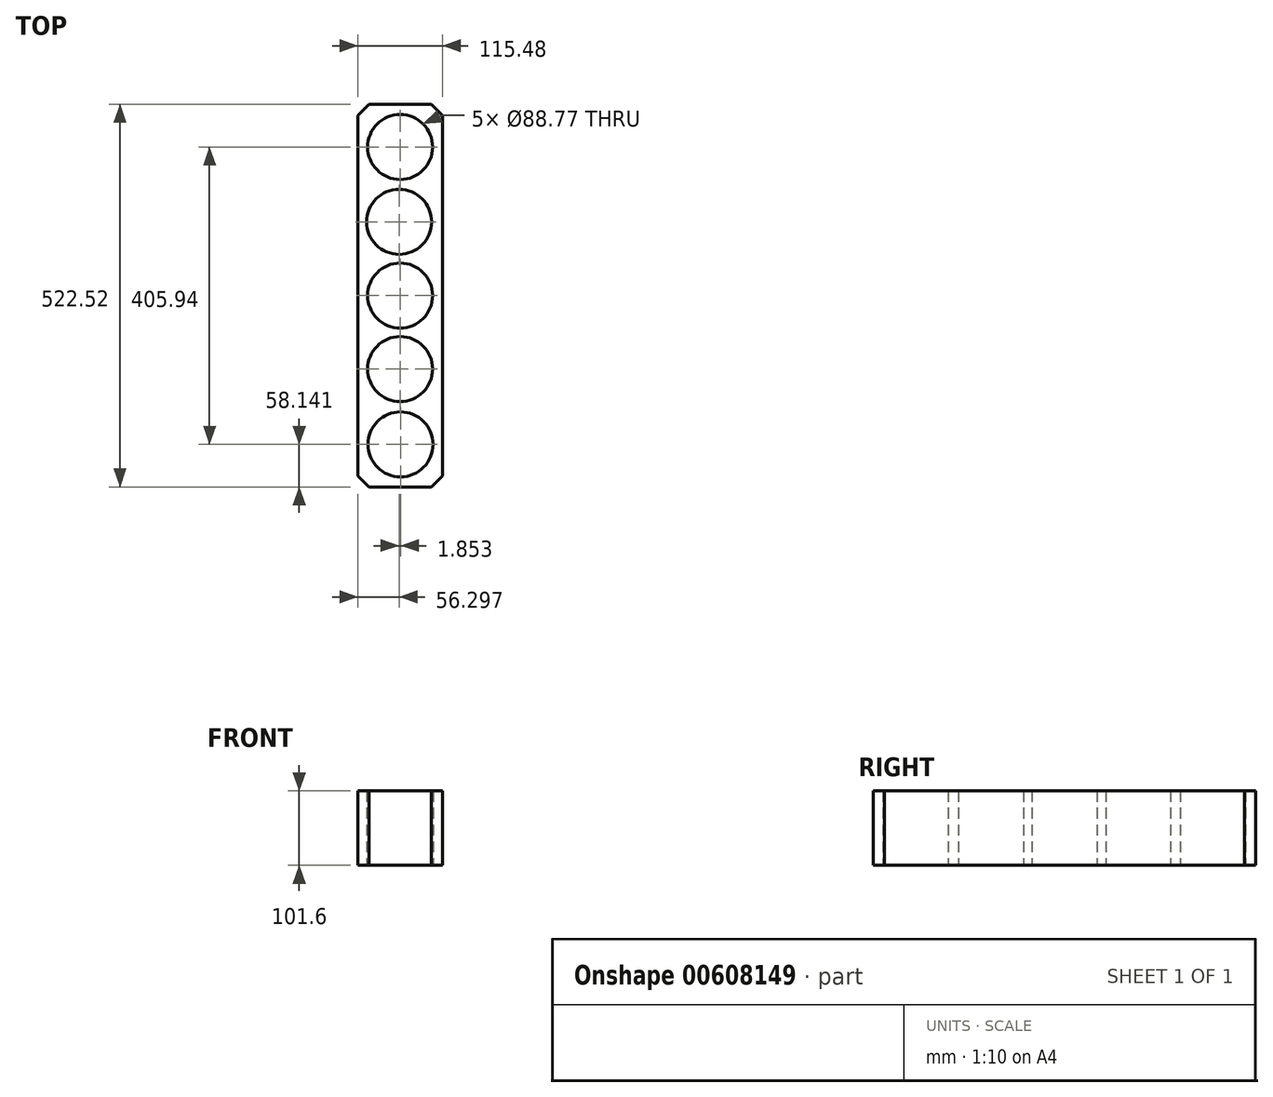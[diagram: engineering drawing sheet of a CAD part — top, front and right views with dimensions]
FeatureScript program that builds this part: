
annotation { "Feature Type Name" : "Feature", "Feature Type Description" : "" }
export const myFeature = defineFeature(function(context is Context, id is Id, definition is map)
    precondition{}
    {
        {
            var Q0;
            Q0=qCreatedBy(makeId("Top.planeOp"),FACE);
            var sketch = newSketch(context, id + "F0", { "sketchPlane" : qUnion([Q0])});
            skLineSegment(sketch, "E0.bottom", {"start": v(-57.74, 261.26) * mm, "end": v(57.74, 261.26) * mm});
            skLineSegment(sketch, "E0.top", {"start": v(-57.74, -261.26) * mm, "end": v(57.74, -261.26) * mm});
            skLineSegment(sketch, "E0.left", {"start": v(-57.74, 261.26) * mm, "end": v(-57.74, -261.26) * mm});
            skLineSegment(sketch, "E0.right", {"start": v(57.74, 261.26) * mm, "end": v(57.74, -261.26) * mm});
            skPoint(sketch, "E0.middle", {"position": v(0, 0) * mm});
            skCircle(sketch, "E1", {"center": v(0, 202.82) * mm, "radius": 44.39 * mm});
            skCircle(sketch, "E2", {"center": v(-1.44, 100.62) * mm, "radius": 44.39 * mm});
            skCircle(sketch, "E3", {"center": v(0, 0) * mm, "radius": 44.39 * mm});
            skCircle(sketch, "E4", {"center": v(0, -100.28) * mm, "radius": 44.39 * mm});
            skCircle(sketch, "E5", {"center": v(0.4, -203.12) * mm, "radius": 44.39 * mm});
            skSolve(sketch);
        }
        {
            var Q0;
            Q0=makeQuery(id+"F0.imprint","IMPRINT",FACE,{"disambiguationData":[TD([[makeQuery(id+"F0.imprint","IMPRINT",EDGE,{"derivedFrom":sQuery(id+"F0.wireOp",EDGE,"E0.bottom")}),-1.0]])]});
            extrude(context, id + "F1", {"entities" : qUnion([Q0]), "depth" : 101.6 * mm, "offsetDistance" : 25.4 * mm});
        }
        {
            var Q0;
            Q0=makeQuery(id+"F1.opExtrude","SWEPT_EDGE",EDGE,{"disambiguationData":[OSD([sQuery(id+"F0.wireOp",EDGE,"E0.top"),sQuery(id+"F0.wireOp",EDGE,"E0.right")])]});
            chamfer(context, id + "F2", {"entities" : qUnion([Q0]), "width" : 15.24 * mm, "tangentPropagation" : true});
        }
        {
            var Q0;
            Q0=makeQuery(id+"F1.opExtrude","SWEPT_EDGE",EDGE,{"disambiguationData":[OSD([sQuery(id+"F0.wireOp",EDGE,"E0.top"),sQuery(id+"F0.wireOp",EDGE,"E0.left")])]});
            chamfer(context, id + "F3", {"entities" : qUnion([Q0]), "width" : 15.24 * mm, "tangentPropagation" : true});
        }
        {
            var Q0;
            Q0=makeQuery(id+"F1.opExtrude","SWEPT_EDGE",EDGE,{"disambiguationData":[OSD([sQuery(id+"F0.wireOp",EDGE,"E0.bottom"),sQuery(id+"F0.wireOp",EDGE,"E0.right")])]});
            chamfer(context, id + "F4", {"entities" : qUnion([Q0]), "width" : 15.24 * mm, "tangentPropagation" : true});
        }
        {
            var Q0;
            Q0=makeQuery(id+"F1.opExtrude","SWEPT_EDGE",EDGE,{"disambiguationData":[OSD([sQuery(id+"F0.wireOp",EDGE,"E0.bottom"),sQuery(id+"F0.wireOp",EDGE,"E0.left")])]});
            chamfer(context, id + "F5", {"entities" : qUnion([Q0]), "width" : 15.24 * mm, "tangentPropagation" : true});
        }
    });
